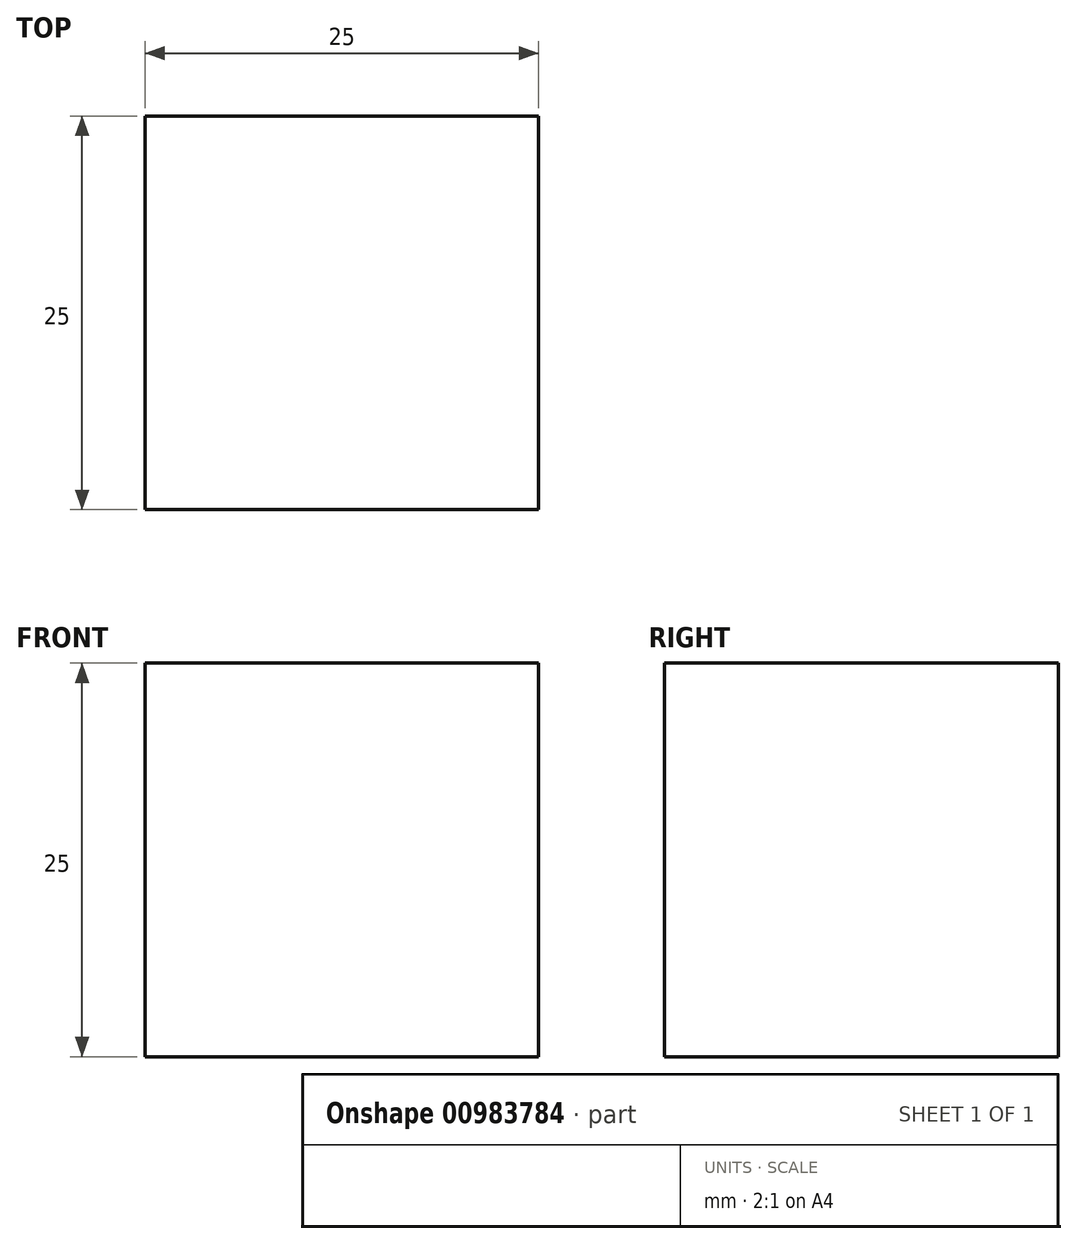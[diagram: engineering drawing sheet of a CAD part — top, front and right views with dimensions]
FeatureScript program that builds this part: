
annotation { "Feature Type Name" : "Feature", "Feature Type Description" : "" }
export const myFeature = defineFeature(function(context is Context, id is Id, definition is map)
    precondition{}
    {
        {
            var Q0;
            Q0=qCreatedBy(makeId("Top.planeOp"),FACE);
            var sketch = newSketch(context, id + "F0", { "sketchPlane" : qUnion([Q0])});
            skLineSegment(sketch, "E0.bottom", {"start": v(-12.5, -12.5) * mm, "end": v(12.5, -12.5) * mm});
            skLineSegment(sketch, "E0.top", {"start": v(-12.5, 12.5) * mm, "end": v(12.5, 12.5) * mm});
            skLineSegment(sketch, "E0.left", {"start": v(-12.5, -12.5) * mm, "end": v(-12.5, 12.5) * mm});
            skLineSegment(sketch, "E0.right", {"start": v(12.5, -12.5) * mm, "end": v(12.5, 12.5) * mm});
            skLineSegment(sketch, "E1", {"start": v(12.5, 12.5) * mm, "end": v(-12.5, -12.5) * mm, "construction": true});
            skSolve(sketch);
        }
        {
            var Q0;
            Q0 = qSketchRegion(id + "F0", true);
            extrude(context, id + "F1", {"entities" : qUnion([Q0]), "depth" : 25 * mm, "offsetDistance" : 25 * mm});
        }
    });
